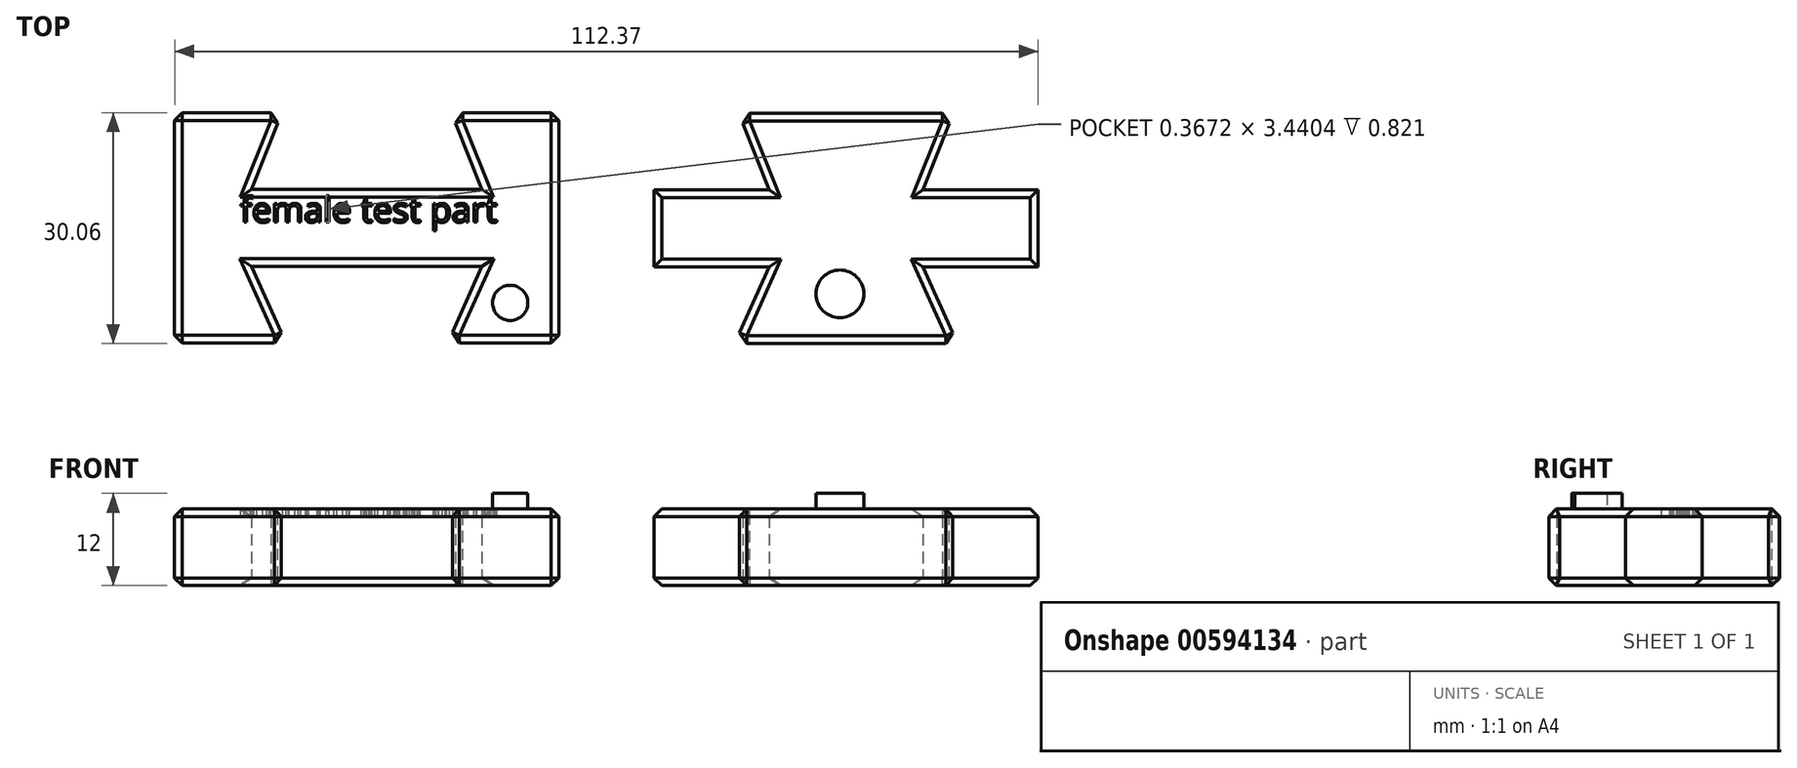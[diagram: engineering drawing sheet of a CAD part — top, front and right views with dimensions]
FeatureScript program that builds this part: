
annotation { "Feature Type Name" : "Feature", "Feature Type Description" : "" }
export const myFeature = defineFeature(function(context is Context, id is Id, definition is map)
    precondition{}
    {
        {
            var Q0;
            Q0=qCreatedBy(makeId("Top.planeOp"),FACE);
            var sketch = newSketch(context, id + "F0", { "sketchPlane" : qUnion([Q0])});
            skLineSegment(sketch, "E0.bottom", {"start": v(10.5, 0) * mm, "end": v(39.5, 0) * mm});
            skLineSegment(sketch, "E0.top", {"start": v(11, 30) * mm, "end": v(39, 30) * mm});
            skLineSegment(sketch, "E0.left", {"start": v(0, 10) * mm, "end": v(0, 20) * mm});
            skLineSegment(sketch, "E0.right", {"start": v(50, 10) * mm, "end": v(50, 20) * mm});
            skPoint(sketch, "E1", {"position": v(0, 10) * mm});
            skPoint(sketch, "E2", {"position": v(15, 10) * mm});
            skPoint(sketch, "E3", {"position": v(10.5, 0) * mm});
            skPoint(sketch, "E4", {"position": v(39.5, 0) * mm});
            skPoint(sketch, "E5", {"position": v(35, 10) * mm});
            skLineSegment(sketch, "E6", {"start": v(0, 10) * mm, "end": v(15, 10) * mm});
            skLineSegment(sketch, "E7", {"start": v(15, 10) * mm, "end": v(10.5, 0) * mm});
            skLineSegment(sketch, "E8", {"start": v(35, 10) * mm, "end": v(50, 10) * mm});
            skLineSegment(sketch, "E9", {"start": v(50, 10) * mm, "end": v(35, 10) * mm});
            skLineSegment(sketch, "E10", {"start": v(39.5, 0) * mm, "end": v(35, 10) * mm});
            skPoint(sketch, "E11.orphan", {"position": v(0, 0) * mm});
            skPoint(sketch, "E12", {"position": v(50, 20) * mm});
            skPoint(sketch, "E13", {"position": v(35, 20) * mm});
            skPoint(sketch, "E14", {"position": v(15, 20) * mm});
            skPoint(sketch, "E15", {"position": v(11, 30) * mm});
            skPoint(sketch, "E16", {"position": v(39, 30) * mm});
            skLineSegment(sketch, "E17", {"start": v(15, 20) * mm, "end": v(11, 30) * mm});
            skLineSegment(sketch, "E18", {"start": v(0, 20) * mm, "end": v(15, 20) * mm});
            skLineSegment(sketch, "E19", {"start": v(35, 20) * mm, "end": v(39, 30) * mm});
            skLineSegment(sketch, "E20", {"start": v(35, 20) * mm, "end": v(50, 20) * mm});
            skPoint(sketch, "E21.orphan", {"position": v(0, 30) * mm});
            skPoint(sketch, "E22.orphan", {"position": v(50, 30) * mm});
            skPoint(sketch, "E23", {"position": v(50, 0) * mm});
            skSolve(sketch);
        }
        {
            var Q0;
            Q0 = qSketchRegion(id + "F0", true);
            extrude(context, id + "F1", {"entities" : qUnion([Q0]), "depth" : 10 * mm, "offsetDistance" : 25 * mm});
        }
        {
            var Q0;
            Q0=makeQuery(id+"F1.opExtrude","CAP_EDGE",EDGE,{"disambiguationData":[OSD([sQuery(id+"F0.wireOp",EDGE,"E0.bottom")])],"isStart":false});
            var Q1;
            Q1=makeQuery(id+"F1.opExtrude","CAP_EDGE",EDGE,{"disambiguationData":[OSD([sQuery(id+"F0.wireOp",EDGE,"E10")])],"isStart":false});
            var Q2;
            Q2=makeQuery(id+"F1.opExtrude","CAP_EDGE",EDGE,{"disambiguationData":[OSD([sQuery(id+"F0.wireOp",EDGE,"E9")])],"isStart":false});
            var Q3;
            Q3=makeQuery(id+"F1.opExtrude","CAP_EDGE",EDGE,{"disambiguationData":[OSD([sQuery(id+"F0.wireOp",EDGE,"E0.right")])],"isStart":false});
            var Q4;
            Q4=makeQuery(id+"F1.opExtrude","CAP_EDGE",EDGE,{"disambiguationData":[OSD([sQuery(id+"F0.wireOp",EDGE,"E20")])],"isStart":false});
            var Q5;
            Q5=makeQuery(id+"F1.opExtrude","CAP_EDGE",EDGE,{"disambiguationData":[OSD([sQuery(id+"F0.wireOp",EDGE,"E19")])],"isStart":false});
            var Q6;
            Q6=makeQuery(id+"F1.opExtrude","CAP_EDGE",EDGE,{"disambiguationData":[OSD([sQuery(id+"F0.wireOp",EDGE,"E0.top")])],"isStart":false});
            var Q7;
            Q7=makeQuery(id+"F1.opExtrude","CAP_FACE",FACE,{"disambiguationData":[OSD([sQuery(id+"F0.wireOp",EDGE,"E0.bottom"),sQuery(id+"F0.wireOp",EDGE,"E0.top"),sQuery(id+"F0.wireOp",EDGE,"E0.left"),sQuery(id+"F0.wireOp",EDGE,"E0.right"),sQuery(id+"F0.wireOp",EDGE,"E6"),sQuery(id+"F0.wireOp",EDGE,"E7"),sQuery(id+"F0.wireOp",EDGE,"E9"),sQuery(id+"F0.wireOp",EDGE,"E10"),sQuery(id+"F0.wireOp",EDGE,"E17"),sQuery(id+"F0.wireOp",EDGE,"E18"),sQuery(id+"F0.wireOp",EDGE,"E19"),sQuery(id+"F0.wireOp",EDGE,"E20")])],"isStart":false});
            var Q8;
            Q8=makeQuery(id+"F1.opExtrude","CAP_FACE",FACE,{"disambiguationData":[OSD([sQuery(id+"F0.wireOp",EDGE,"E0.bottom"),sQuery(id+"F0.wireOp",EDGE,"E0.top"),sQuery(id+"F0.wireOp",EDGE,"E0.left"),sQuery(id+"F0.wireOp",EDGE,"E0.right"),sQuery(id+"F0.wireOp",EDGE,"E6"),sQuery(id+"F0.wireOp",EDGE,"E7"),sQuery(id+"F0.wireOp",EDGE,"E9"),sQuery(id+"F0.wireOp",EDGE,"E10"),sQuery(id+"F0.wireOp",EDGE,"E17"),sQuery(id+"F0.wireOp",EDGE,"E18"),sQuery(id+"F0.wireOp",EDGE,"E19"),sQuery(id+"F0.wireOp",EDGE,"E20")])],"isStart":true});
            var Q9;
            Q9=makeQuery(id+"F1.opExtrude","SWEPT_EDGE",EDGE,{"disambiguationData":[OSD([sQuery(id+"F0.wireOp",EDGE,"E0.bottom"),sQuery(id+"F0.wireOp",EDGE,"E7")])]});
            var Q10;
            Q10=makeQuery(id+"F1.opExtrude","SWEPT_EDGE",EDGE,{"disambiguationData":[OSD([sQuery(id+"F0.wireOp",EDGE,"E0.bottom"),sQuery(id+"F0.wireOp",EDGE,"E10")])]});
            var Q11;
            Q11=makeQuery(id+"F1.opExtrude","SWEPT_FACE",FACE,{"disambiguationData":[OSD([sQuery(id+"F0.wireOp",EDGE,"E0.top")])]});
            chamfer(context, id + "F2", {"entities" : qUnion([Q0, Q1, Q2, Q3, Q4, Q5, Q6, Q7, Q8, Q9, Q10, Q11]), "width" : 1 * mm, "tangentPropagation" : true});
        }
        {
            var Q0;
            Q0=qCreatedBy(makeId("Top.planeOp"),FACE);
            var sketch = newSketch(context, id + "F3", { "sketchPlane" : qUnion([Q0])});
            skLineSegment(sketch, "E24.left", {"start": v(-62.37, 10.06) * mm, "end": v(-62.37, 20.06) * mm});
            skLineSegment(sketch, "E24.right", {"start": v(-12.37, 10.06) * mm, "end": v(-12.37, 20.06) * mm});
            skPoint(sketch, "E25", {"position": v(-62.37, 10.06) * mm});
            skPoint(sketch, "E26", {"position": v(-52.37, 10.06) * mm});
            skPoint(sketch, "E27", {"position": v(-47.87, 0.06) * mm});
            skPoint(sketch, "E28.orphan", {"position": v(-62.37, 0.06) * mm});
            skPoint(sketch, "E29", {"position": v(-12.37, 20.06) * mm});
            skPoint(sketch, "E30", {"position": v(-22.37, 20.06) * mm});
            skPoint(sketch, "E31", {"position": v(-52.37, 20.06) * mm});
            skPoint(sketch, "E32", {"position": v(-48.37, 30.06) * mm});
            skPoint(sketch, "E33", {"position": v(-26.37, 30.06) * mm});
            skLineSegment(sketch, "E34", {"start": v(-52.37, 20.06) * mm, "end": v(-48.37, 30.06) * mm});
            skLineSegment(sketch, "E35", {"start": v(-22.37, 20.06) * mm, "end": v(-26.37, 30.06) * mm});
            skPoint(sketch, "E36.orphan", {"position": v(-62.37, 30.06) * mm});
            skPoint(sketch, "E37.orphan", {"position": v(-12.37, 30.06) * mm});
            skPoint(sketch, "E38", {"position": v(-12.37, 0.06) * mm});
            skPoint(sketch, "E39", {"position": v(-26.87, 0.06) * mm});
            skLineSegment(sketch, "E40", {"start": v(-12.37, 10.06) * mm, "end": v(-12.37, 0.06) * mm});
            skLineSegment(sketch, "E41", {"start": v(-12.37, 0.06) * mm, "end": v(-26.87, 0.06) * mm});
            skPoint(sketch, "E42.end.orphan", {"position": v(-22.37, 10.06) * mm});
            skLineSegment(sketch, "E43", {"start": v(-62.37, 10.06) * mm, "end": v(-62.37, 0.06) * mm});
            skLineSegment(sketch, "E44", {"start": v(-62.37, 0.06) * mm, "end": v(-47.87, 0.06) * mm});
            skLineSegment(sketch, "E45", {"start": v(-26.87, 0.06) * mm, "end": v(-22.37, 10.06) * mm});
            skLineSegment(sketch, "E46", {"start": v(-22.37, 10.06) * mm, "end": v(-52.37, 10.06) * mm});
            skLineSegment(sketch, "E47", {"start": v(-47.87, 0.06) * mm, "end": v(-52.37, 10.06) * mm});
            skPoint(sketch, "E48.orphan", {"position": v(-30.87, 0.06) * mm});
            skLineSegment(sketch, "E49", {"start": v(-12.37, 20.06) * mm, "end": v(-12.37, 30.06) * mm});
            skLineSegment(sketch, "E50", {"start": v(-12.37, 30.06) * mm, "end": v(-26.37, 30.06) * mm});
            skLineSegment(sketch, "E51", {"start": v(-48.37, 30.06) * mm, "end": v(-62.37, 30.06) * mm});
            skLineSegment(sketch, "E52", {"start": v(-62.37, 30.06) * mm, "end": v(-62.37, 20.06) * mm});
            skLineSegment(sketch, "E53", {"start": v(-22.37, 20.06) * mm, "end": v(-52.37, 20.06) * mm});
            skSolve(sketch);
        }
        {
            var Q0;
            Q0=makeQuery(id+"F3.imprint","IMPRINT",FACE,{"disambiguationData":[TD([[makeQuery(id+"F3.imprint","IMPRINT",EDGE,{"derivedFrom":sQuery(id+"F3.wireOp",EDGE,"E24.left")}),-1.0]])]});
            extrude(context, id + "F4", {"entities" : qUnion([Q0]), "depth" : 10 * mm, "offsetDistance" : 25 * mm});
        }
        {
            var Q0;
            Q0=makeQuery(id+"F4.opExtrude","CAP_FACE",FACE,{"disambiguationData":[OSD([sQuery(id+"F3.wireOp",EDGE,"E24.left"),sQuery(id+"F3.wireOp",EDGE,"E24.right"),sQuery(id+"F3.wireOp",EDGE,"E34"),sQuery(id+"F3.wireOp",EDGE,"E35"),sQuery(id+"F3.wireOp",EDGE,"E40"),sQuery(id+"F3.wireOp",EDGE,"E41"),sQuery(id+"F3.wireOp",EDGE,"E43"),sQuery(id+"F3.wireOp",EDGE,"E44"),sQuery(id+"F3.wireOp",EDGE,"E45"),sQuery(id+"F3.wireOp",EDGE,"E46"),sQuery(id+"F3.wireOp",EDGE,"E47"),sQuery(id+"F3.wireOp",EDGE,"E49"),sQuery(id+"F3.wireOp",EDGE,"E50"),sQuery(id+"F3.wireOp",EDGE,"E51"),sQuery(id+"F3.wireOp",EDGE,"E52"),sQuery(id+"F3.wireOp",EDGE,"E53")])],"isStart":false});
            var Q1;
            Q1=makeQuery(id+"F4.opExtrude","SWEPT_FACE",FACE,{"disambiguationData":[OSD([sQuery(id+"F3.wireOp",EDGE,"E50")])]});
            var Q2;
            Q2=makeQuery(id+"F4.opExtrude","SWEPT_FACE",FACE,{"disambiguationData":[OSD([sQuery(id+"F3.wireOp",EDGE,"E51")])]});
            var Q3;
            Q3=makeQuery(id+"F4.opExtrude","CAP_FACE",FACE,{"disambiguationData":[OSD([sQuery(id+"F3.wireOp",EDGE,"E24.left"),sQuery(id+"F3.wireOp",EDGE,"E24.right"),sQuery(id+"F3.wireOp",EDGE,"E34"),sQuery(id+"F3.wireOp",EDGE,"E35"),sQuery(id+"F3.wireOp",EDGE,"E40"),sQuery(id+"F3.wireOp",EDGE,"E41"),sQuery(id+"F3.wireOp",EDGE,"E43"),sQuery(id+"F3.wireOp",EDGE,"E44"),sQuery(id+"F3.wireOp",EDGE,"E45"),sQuery(id+"F3.wireOp",EDGE,"E46"),sQuery(id+"F3.wireOp",EDGE,"E47"),sQuery(id+"F3.wireOp",EDGE,"E49"),sQuery(id+"F3.wireOp",EDGE,"E50"),sQuery(id+"F3.wireOp",EDGE,"E51"),sQuery(id+"F3.wireOp",EDGE,"E52"),sQuery(id+"F3.wireOp",EDGE,"E53")])],"isStart":true});
            var Q4;
            Q4=makeQuery(id+"F4.opExtrude","SWEPT_FACE",FACE,{"disambiguationData":[OSD([sQuery(id+"F3.wireOp",EDGE,"E41")])]});
            var Q5;
            Q5=makeQuery(id+"F4.opExtrude","SWEPT_FACE",FACE,{"disambiguationData":[OSD([sQuery(id+"F3.wireOp",EDGE,"E44")])]});
            chamfer(context, id + "F5", {"entities" : qUnion([Q0, Q1, Q2, Q3, Q4, Q5]), "width" : 1 * mm, "tangentPropagation" : true});
        }
        {
            var Q0;
            Q0=makeQuery(id+"F1.opExtrude","CAP_FACE",FACE,{"disambiguationData":[OSD([sQuery(id+"F0.wireOp",EDGE,"E0.bottom"),sQuery(id+"F0.wireOp",EDGE,"E0.top"),sQuery(id+"F0.wireOp",EDGE,"E0.left"),sQuery(id+"F0.wireOp",EDGE,"E0.right"),sQuery(id+"F0.wireOp",EDGE,"E6"),sQuery(id+"F0.wireOp",EDGE,"E7"),sQuery(id+"F0.wireOp",EDGE,"E9"),sQuery(id+"F0.wireOp",EDGE,"E10"),sQuery(id+"F0.wireOp",EDGE,"E17"),sQuery(id+"F0.wireOp",EDGE,"E18"),sQuery(id+"F0.wireOp",EDGE,"E19"),sQuery(id+"F0.wireOp",EDGE,"E20")])],"isStart":false});
            var sketch = newSketch(context, id + "F6", { "sketchPlane" : qUnion([Q0])});
            skCircle(sketch, "E54", {"center": v(24.2, 6.47) * mm, "radius": 3.1 * mm});
            skSolve(sketch);
        }
        {
            var Q0;
            Q0=makeQuery(id+"F4.opExtrude","CAP_FACE",FACE,{"disambiguationData":[OSD([sQuery(id+"F3.wireOp",EDGE,"E24.left"),sQuery(id+"F3.wireOp",EDGE,"E24.right"),sQuery(id+"F3.wireOp",EDGE,"E34"),sQuery(id+"F3.wireOp",EDGE,"E35"),sQuery(id+"F3.wireOp",EDGE,"E40"),sQuery(id+"F3.wireOp",EDGE,"E41"),sQuery(id+"F3.wireOp",EDGE,"E43"),sQuery(id+"F3.wireOp",EDGE,"E44"),sQuery(id+"F3.wireOp",EDGE,"E45"),sQuery(id+"F3.wireOp",EDGE,"E46"),sQuery(id+"F3.wireOp",EDGE,"E47"),sQuery(id+"F3.wireOp",EDGE,"E49"),sQuery(id+"F3.wireOp",EDGE,"E50"),sQuery(id+"F3.wireOp",EDGE,"E51"),sQuery(id+"F3.wireOp",EDGE,"E52"),sQuery(id+"F3.wireOp",EDGE,"E53")])],"isStart":false});
            var sketch = newSketch(context, id + "F7", { "sketchPlane" : qUnion([Q0])});
            skCircle(sketch, "E55", {"center": v(-18.7, 5.3) * mm, "radius": 2.3 * mm});
            skSolve(sketch);
        }
        {
            var Q0;
            Q0=makeQuery(id+"F7.imprint","IMPRINT",FACE,{"disambiguationData":[TD([[makeQuery(id+"F7.imprint","IMPRINT",EDGE,{"derivedFrom":sQuery(id+"F7.wireOp",EDGE,"E55")}),1.0]])]});
            var Q1;
            Q1=makeQuery(id+"F6.imprint","IMPRINT",FACE,{"disambiguationData":[TD([[makeQuery(id+"F6.imprint","IMPRINT",EDGE,{"derivedFrom":sQuery(id+"F6.wireOp",EDGE,"E54")}),1.0]])]});
            extrude(context, id + "F8", {"entities" : qUnion([Q0, Q1]), "depth" : 2 * mm, "offsetDistance" : 25 * mm});
        }
        {
            var Q0;
            Q0=makeQuery(id+"F4.opExtrude","CAP_FACE",FACE,{"disambiguationData":[OSD([sQuery(id+"F3.wireOp",EDGE,"E24.left"),sQuery(id+"F3.wireOp",EDGE,"E24.right"),sQuery(id+"F3.wireOp",EDGE,"E34"),sQuery(id+"F3.wireOp",EDGE,"E35"),sQuery(id+"F3.wireOp",EDGE,"E40"),sQuery(id+"F3.wireOp",EDGE,"E41"),sQuery(id+"F3.wireOp",EDGE,"E43"),sQuery(id+"F3.wireOp",EDGE,"E44"),sQuery(id+"F3.wireOp",EDGE,"E45"),sQuery(id+"F3.wireOp",EDGE,"E46"),sQuery(id+"F3.wireOp",EDGE,"E47"),sQuery(id+"F3.wireOp",EDGE,"E49"),sQuery(id+"F3.wireOp",EDGE,"E50"),sQuery(id+"F3.wireOp",EDGE,"E51"),sQuery(id+"F3.wireOp",EDGE,"E52"),sQuery(id+"F3.wireOp",EDGE,"E53")])],"isStart":false});
            var sketch = newSketch(context, id + "F9", { "sketchPlane" : qUnion([Q0])});
            skText(sketch, "E56", { "text": "female test part", "fontName": "OpenSans-Regular.ttf"});
            const initialGuessF9  = {"E56": [-0.05385, 0.0158, 1, 0, 0.00326]};
            skSetInitialGuess(sketch, initialGuessF9);
            skSolve(sketch);
        }
        {
            var Q0;
            Q0 = qSketchRegion(id + "F9", true);
            extrude(context, id + "F10", {"entities" : qUnion([Q0]), "operationType" : NewBodyOperationType.REMOVE, "oppositeDirection" : true, "depth" : 1 * mm, "offsetDistance" : 25 * mm});
        }
    });
